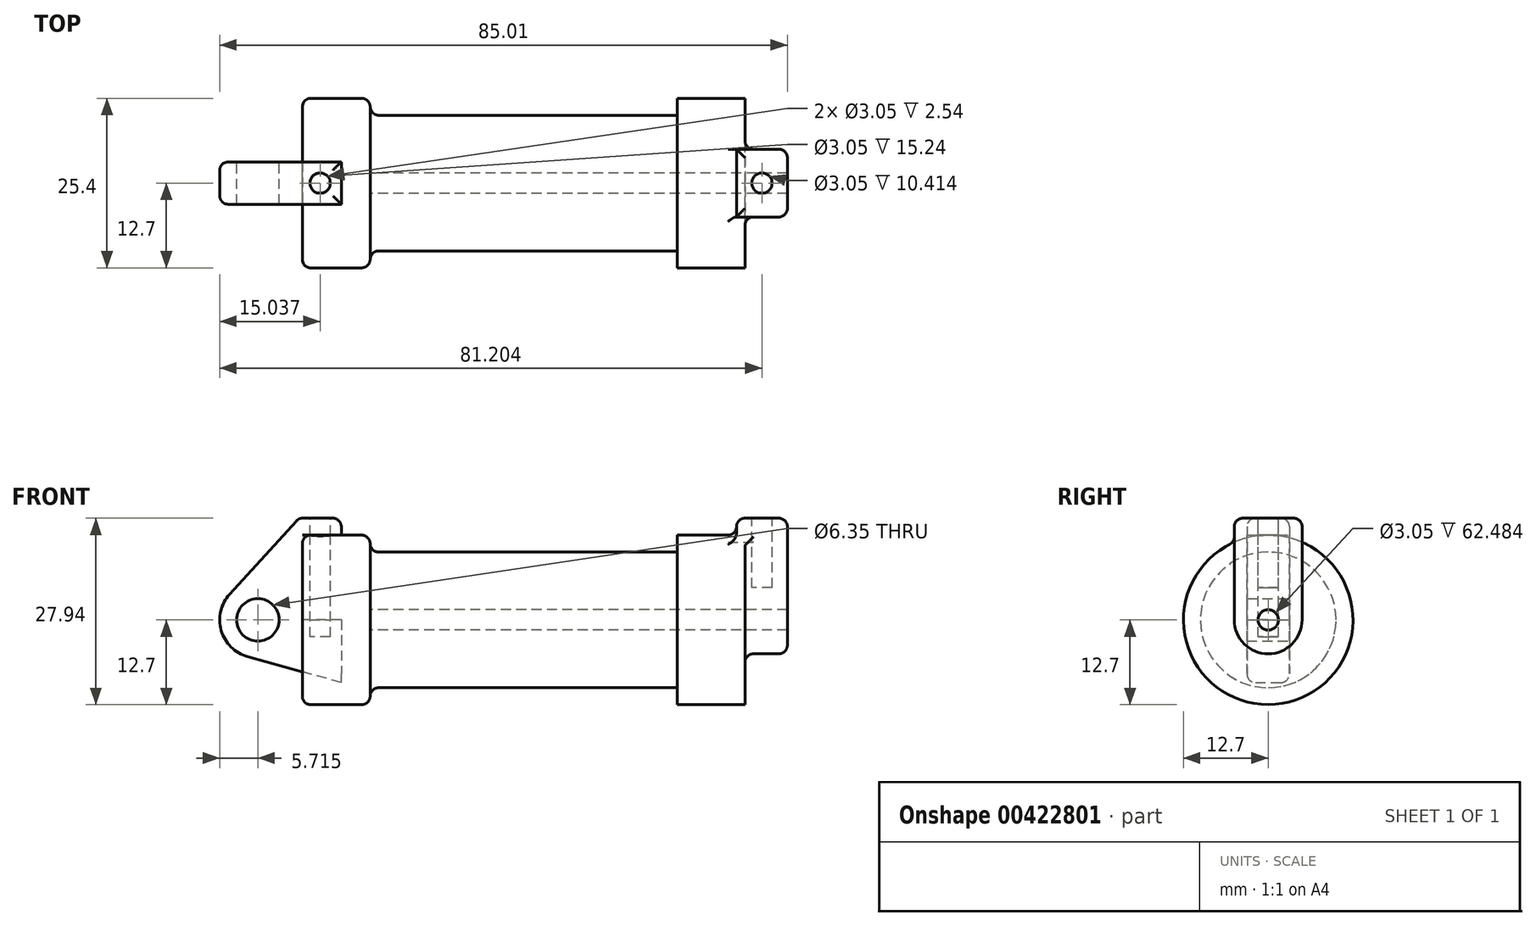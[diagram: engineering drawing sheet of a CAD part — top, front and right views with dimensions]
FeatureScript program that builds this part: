
annotation { "Feature Type Name" : "Feature", "Feature Type Description" : "" }
export const myFeature = defineFeature(function(context is Context, id is Id, definition is map)
    precondition{}
    {
        {
            var Q0;
            Q0=qCreatedBy(makeId("Front.planeOp"),FACE);
            var sketch = newSketch(context, id + "F0", { "sketchPlane" : qUnion([Q0])});
            skLineSegment(sketch, "E0", {"start": v(0, 0) * mm, "end": v(0, 12.7) * mm});
            skLineSegment(sketch, "E1", {"start": v(0, 12.7) * mm, "end": v(10.16, 12.7) * mm});
            skLineSegment(sketch, "E2", {"start": v(10.16, 12.7) * mm, "end": v(10.16, 10.16) * mm});
            skLineSegment(sketch, "E3", {"start": v(10.16, 10.16) * mm, "end": v(56.13, 10.16) * mm});
            skLineSegment(sketch, "E4", {"start": v(56.13, 10.16) * mm, "end": v(56.13, 12.7) * mm});
            skLineSegment(sketch, "E5", {"start": v(56.13, 12.7) * mm, "end": v(66.3, 12.7) * mm});
            skLineSegment(sketch, "E6", {"start": v(66.3, 12.7) * mm, "end": v(66.3, 0) * mm});
            skLineSegment(sketch, "E7", {"start": v(66.3, 0) * mm, "end": v(0, 0) * mm});
            skLineSegment(sketch, "E8", {"start": v(5.84, 15.24) * mm, "end": v(-0.5, 15.24) * mm});
            skLineSegment(sketch, "E9", {"start": v(-0.5, 15.24) * mm, "end": v(-10.88, 3.85) * mm});
            skLineSegment(sketch, "E10", {"start": v(0, 0) * mm, "end": v(-6.65, 0) * mm});
            skCircle(sketch, "E11", {"center": v(-6.65, 0) * mm, "radius": 5.72 * mm});
            skCircle(sketch, "E12", {"center": v(-6.65, 0) * mm, "radius": 3.18 * mm});
            skLineSegment(sketch, "E13", {"start": v(5.84, 15.24) * mm, "end": v(5.84, -9.4) * mm});
            skLineSegment(sketch, "E14", {"start": v(5.84, -9.4) * mm, "end": v(-8.18, -5.5) * mm});
            skSolve(sketch);
        }
        {
            var Q0;
            {var subQ0=sQuery(id+"F0.wireOp",EDGE,"E2");Q0=makeQuery(id+"F0.imprint","IMPRINT",FACE,{"disambiguationData":[TD([[makeQuery(id+"F0.imprint","IMPRINT",EDGE,{"derivedFrom":subQ0}),-1.0]])]});}
            var Q1;
            {var subQ0=sQuery(id+"F0.wireOp",EDGE,"E0");Q1=makeQuery(id+"F0.imprint","IMPRINT",FACE,{"disambiguationData":[TD([[makeQuery(id+"F0.imprint","IMPRINT",EDGE,{"derivedFrom":subQ0}),-1.0]])]});}
            var Q2;
            Q2=sQuery(id+"F0.wireOp",EDGE,"E7");
            revolve(context, id + "F1", {"entities" : qUnion([Q0, Q1]), "axis" : qUnion([Q2]), "revolveType" : RevolveType.FULL});
        }
        {
            var Q0;
            {var subQ1=sQuery(id+"F0.wireOp",EDGE,"E0");Q0=makeQuery(id+"F0.imprint","IMPRINT",FACE,{"disambiguationData":[TD([[makeQuery(id+"F0.imprint","IMPRINT",EDGE,{"derivedFrom":subQ1}),1.0]])]});}
            var Q1;
            {var subQ5=sQuery(id+"F0.wireOp",EDGE,"E12");Q1=makeQuery(id+"F0.imprint","IMPRINT",FACE,{"disambiguationData":[TD([[makeQuery(id+"F0.imprint","IMPRINT",EDGE,{"derivedFrom":subQ5}),-1.0]])]});}
            var Q2;
            {var subQ0=sQuery(id+"F0.wireOp",EDGE,"E14");Q2=makeQuery(id+"F0.imprint","IMPRINT",FACE,{"disambiguationData":[TD([[makeQuery(id+"F0.imprint","IMPRINT",EDGE,{"derivedFrom":subQ0}),-1.0]])]});}
            extrude(context, id + "F2", {"entities" : qUnion([Q0, Q1, Q2]), "endBound" : BoundingType.SYMMETRIC, "depth" : 6.35 * mm});
        }
        {
            var Q0;
            Q0=makeQuery(id+"F1.opRevolve","SWEPT_FACE",FACE,{"disambiguationData":[OSD([sQuery(id+"F0.wireOp",EDGE,"E6")])]});
            var sketch = newSketch(context, id + "F3", { "sketchPlane" : qUnion([Q0])});
            skCircle(sketch, "E15", {"center": v(0, 0) * mm, "radius": 1.52 * mm});
            skCircle(sketch, "E16", {"center": v(0, 0) * mm, "radius": 5.08 * mm});
            skLineSegment(sketch, "E17", {"start": v(-5.08, 0) * mm, "end": v(-5.08, 15.24) * mm});
            skLineSegment(sketch, "E18", {"start": v(5.08, 0) * mm, "end": v(5.08, 15.24) * mm});
            skLineSegment(sketch, "E19", {"start": v(-5.08, 15.24) * mm, "end": v(5.08, 15.24) * mm});
            skSolve(sketch);
        }
        {
            var Q0;
            Q0 = qSketchRegion(id + "F3", true);
            extrude(context, id + "F4", {"entities" : qUnion([Q0]), "operationType" : NewBodyOperationType.ADD, "oppositeDirection" : true, "depth" : 1.27 * mm});
        }
        {
            var Q0;
            {var subQ0=sQuery(id+"F3.wireOp",EDGE,"E17");var subQ1=sQuery(id+"F3.wireOp",EDGE,"E16");var subQ2=makeQuery(id+"F3.imprint","INTERSECT",VERTEX,{"derivedFrom":[subQ1,subQ0]});Q0=makeQuery(id+"F3.imprint","IMPRINT",FACE,{"disambiguationData":[TD([[makeQuery(id+"F3.imprint","IMPRINT",EDGE,{"disambiguationData":[TD([[subQ2,1.0]])],"derivedFrom":subQ1}),-1.0]])]});}
            var Q1;
            {var subQ0=sQuery(id+"F3.wireOp",EDGE,"E19");Q1=makeQuery(id+"F3.imprint","IMPRINT",FACE,{"disambiguationData":[TD([[makeQuery(id+"F3.imprint","IMPRINT",EDGE,{"derivedFrom":subQ0}),-1.0]])]});}
            var Q2;
            Q2=makeQuery(id+"F3.imprint","IMPRINT",FACE,{"disambiguationData":[TD([[makeQuery(id+"F3.imprint","IMPRINT",EDGE,{"derivedFrom":sQuery(id+"F3.wireOp",EDGE,"E15")}),-1.0]])]});
            extrude(context, id + "F5", {"entities" : qUnion([Q0, Q1, Q2]), "operationType" : NewBodyOperationType.ADD, "depth" : 6.35 * mm});
        }
        {
            var Q0;
            Q0=makeQuery(id+"F3.imprint","IMPRINT",FACE,{"disambiguationData":[TD([[makeQuery(id+"F3.imprint","IMPRINT",EDGE,{"derivedFrom":sQuery(id+"F3.wireOp",EDGE,"E15")}),1.0]])]});
            var Q1;
            Q1=makeQuery(id+"F1.opRevolve","SWEPT_FACE",FACE,{"disambiguationData":[OSD([sQuery(id+"F0.wireOp",EDGE,"E2")])]});
            extrude(context, id + "F6", {"entities" : qUnion([Q0]), "operationType" : NewBodyOperationType.REMOVE, "endBound" : BoundingType.UP_TO_SURFACE, "oppositeDirection" : true, "endBoundEntityFace" : qUnion([Q1]), "depth" : 25.4 * mm});
        }
        {
            var Q0;
            Q0=makeQuery(id+"F2.opExtrude","SWEPT_FACE",FACE,{"disambiguationData":[OSD([sQuery(id+"F0.wireOp",EDGE,"E8")])]});
            var sketch = newSketch(context, id + "F7", { "sketchPlane" : qUnion([Q0])});
            skCircle(sketch, "E20", {"center": v(2.67, 0) * mm, "radius": 1.52 * mm});
            skPoint(sketch, "E20.centerSnap0", {"position": v(2.67, 3.18) * mm});
            skPoint(sketch, "E20.centerSnap1", {"position": v(5.84, 0) * mm});
            skSolve(sketch);
        }
        {
            var Q0;
            {var subQ0=sQuery(id+"F3.wireOp",EDGE,"E19");Q0=makeQuery(id+"F5.boolean.opBoolean","MERGE",FACE,{"derivedFrom":[makeQuery(id+"F4.opExtrude","SWEPT_FACE",FACE,{"disambiguationData":[OSD([subQ0])]}),makeQuery(id+"F5.opExtrude","SWEPT_FACE",FACE,{"disambiguationData":[OSD([subQ0])]})]});}
            var sketch = newSketch(context, id + "F8", { "sketchPlane" : qUnion([Q0])});
            skCircle(sketch, "E21", {"center": v(68.83, 0) * mm, "radius": 1.52 * mm});
            skSolve(sketch);
        }
        {
            var Q0;
            Q0=makeQuery(id+"F7.imprint","IMPRINT",FACE,{"disambiguationData":[TD([[makeQuery(id+"F7.imprint","IMPRINT",EDGE,{"derivedFrom":sQuery(id+"F7.wireOp",EDGE,"E20")}),1.0]])]});
            var Q1;
            Q1=sQuery(id+"F7.wireOp",EDGE,"E20");
            var Q2;
            Q2=makeQuery(id+"F1.opRevolve","SWEPT_FACE",FACE,{"disambiguationData":[OSD([sQuery(id+"F0.wireOp",EDGE,"E1")])]});
            extrude(context, id + "F9", {"entities" : qUnion([Q0]), "operationType" : NewBodyOperationType.REMOVE, "surfaceEntities" : qUnion([Q1]), "oppositeDirection" : true, "endBoundEntityFace" : qUnion([Q2]), "depth" : 17.78 * mm});
        }
        {
            var Q0;
            Q0=makeQuery(id+"F8.imprint","IMPRINT",FACE,{"disambiguationData":[TD([[makeQuery(id+"F8.imprint","IMPRINT",EDGE,{"derivedFrom":sQuery(id+"F8.wireOp",EDGE,"E21")}),1.0]])]});
            var Q1;
            Q1=sQuery(id+"F8.wireOp",EDGE,"E21");
            extrude(context, id + "F10", {"entities" : qUnion([Q0]), "operationType" : NewBodyOperationType.REMOVE, "surfaceEntities" : qUnion([Q1]), "oppositeDirection" : true, "depth" : 10.4 * mm});
        }
        {
            var Q0;
            Q0=makeQuery(id+"F1.opRevolve","SWEPT_EDGE",EDGE,{"disambiguationData":[OSD([sQuery(id+"F0.wireOp",EDGE,"E1"),sQuery(id+"F0.wireOp",EDGE,"E2")])]});
            var Q1;
            Q1=makeQuery(id+"F1.opRevolve","SWEPT_EDGE",EDGE,{"disambiguationData":[OSD([sQuery(id+"F0.wireOp",EDGE,"E2"),sQuery(id+"F0.wireOp",EDGE,"E3")])]});
            var Q2;
            Q2=makeQuery(id+"F1.opRevolve","SWEPT_EDGE",EDGE,{"disambiguationData":[OSD([sQuery(id+"F0.wireOp",EDGE,"E0"),sQuery(id+"F0.wireOp",EDGE,"E1")])]});
            var Q3;
            Q3=makeQuery(id+"F2.opExtrude","CAP_EDGE",EDGE,{"disambiguationData":[OSD([sQuery(id+"F0.wireOp",EDGE,"E9")])],"isStart":false});
            var Q4;
            Q4=makeQuery(id+"F2.opExtrude","CAP_EDGE",EDGE,{"disambiguationData":[OSD([sQuery(id+"F0.wireOp",EDGE,"E9")])],"isStart":true});
            var Q5;
            Q5=makeQuery(id+"F2.opExtrude","CAP_EDGE",EDGE,{"disambiguationData":[OSD([sQuery(id+"F0.wireOp",EDGE,"E8")])],"isStart":false});
            var Q6;
            Q6=makeQuery(id+"F2.opExtrude","CAP_EDGE",EDGE,{"disambiguationData":[OSD([sQuery(id+"F0.wireOp",EDGE,"E8")])],"isStart":true});
            var Q7;
            Q7=makeQuery(id+"F2.opExtrude","SWEPT_EDGE",EDGE,{"disambiguationData":[OSD([sQuery(id+"F0.wireOp",EDGE,"E8"),sQuery(id+"F0.wireOp",EDGE,"E13")])]});
            var Q8;
            Q8=makeQuery(id+"F2.opExtrude","SWEPT_EDGE",EDGE,{"disambiguationData":[OSD([sQuery(id+"F0.wireOp",EDGE,"E8"),sQuery(id+"F0.wireOp",EDGE,"E9")])]});
            fillet(context, id + "F11", {"entities" : qUnion([Q0, Q1, Q2, Q3, Q4, Q5, Q6, Q7, Q8]), "radius" : 1.27 * mm, "tangentPropagation" : true, "allowEdgeOverflow" : false});
        }
        {
            var Q0;
            {var subQ0=sQuery(id+"F3.wireOp",EDGE,"E19");var subQ1=sQuery(id+"F3.wireOp",EDGE,"E17");Q0=makeQuery(id+"F5.boolean.opBoolean","MERGE",EDGE,{"derivedFrom":[makeQuery(id+"F4.opExtrude","SWEPT_EDGE",EDGE,{"disambiguationData":[OSD([subQ1,subQ0])]}),makeQuery(id+"F5.opExtrude","SWEPT_EDGE",EDGE,{"disambiguationData":[OSD([subQ1,subQ0])]})]});}
            var Q1;
            Q1=makeQuery(id+"F4.opExtrude","CAP_EDGE",EDGE,{"disambiguationData":[OSD([sQuery(id+"F3.wireOp",EDGE,"E19")])],"isStart":false});
            var Q2;
            Q2=makeQuery(id+"F5.opExtrude","CAP_EDGE",EDGE,{"disambiguationData":[OSD([sQuery(id+"F3.wireOp",EDGE,"E19")])],"isStart":false});
            var Q3;
            {var subQ0=sQuery(id+"F3.wireOp",EDGE,"E19");var subQ1=sQuery(id+"F3.wireOp",EDGE,"E18");Q3=makeQuery(id+"F5.boolean.opBoolean","MERGE",EDGE,{"derivedFrom":[makeQuery(id+"F4.opExtrude","SWEPT_EDGE",EDGE,{"disambiguationData":[OSD([subQ1,subQ0])]}),makeQuery(id+"F5.opExtrude","SWEPT_EDGE",EDGE,{"disambiguationData":[OSD([subQ1,subQ0])]})]});}
            var Q4;
            Q4=makeQuery(id+"F5.opExtrude","CAP_EDGE",EDGE,{"disambiguationData":[OSD([sQuery(id+"F3.wireOp",EDGE,"E17")])],"isStart":true});
            var Q5;
            Q5=makeQuery(id+"F4.boolean.opBoolean","INTERSECT",EDGE,{"derivedFrom":[makeQuery(id+"F1.opRevolve","SWEPT_FACE",FACE,{"disambiguationData":[OSD([sQuery(id+"F0.wireOp",EDGE,"E5")])]}),makeQuery(id+"F4.opExtrude","SWEPT_FACE",FACE,{"disambiguationData":[OSD([sQuery(id+"F3.wireOp",EDGE,"E17")])]})]});
            var Q6;
            Q6=makeQuery(id+"F5.opExtrude","CAP_EDGE",EDGE,{"disambiguationData":[OSD([sQuery(id+"F3.wireOp",EDGE,"E17")])],"isStart":false});
            var Q7;
            Q7=makeQuery(id+"F4.boolean.opBoolean","INTERSECT",EDGE,{"derivedFrom":[makeQuery(id+"F1.opRevolve","SWEPT_FACE",FACE,{"disambiguationData":[OSD([sQuery(id+"F0.wireOp",EDGE,"E5")])]}),makeQuery(id+"F4.opExtrude","CAP_FACE",FACE,{"disambiguationData":[OSD([sQuery(id+"F3.wireOp",EDGE,"E15"),sQuery(id+"F3.wireOp",EDGE,"E16"),sQuery(id+"F3.wireOp",EDGE,"E17"),sQuery(id+"F3.wireOp",EDGE,"E18"),sQuery(id+"F3.wireOp",EDGE,"E19")])],"isStart":false})]});
            fillet(context, id + "F12", {"entities" : qUnion([Q0, Q1, Q2, Q3, Q4, Q5, Q6, Q7]), "radius" : 1.27 * mm, "tangentPropagation" : true, "allowEdgeOverflow" : false});
        }
    });
